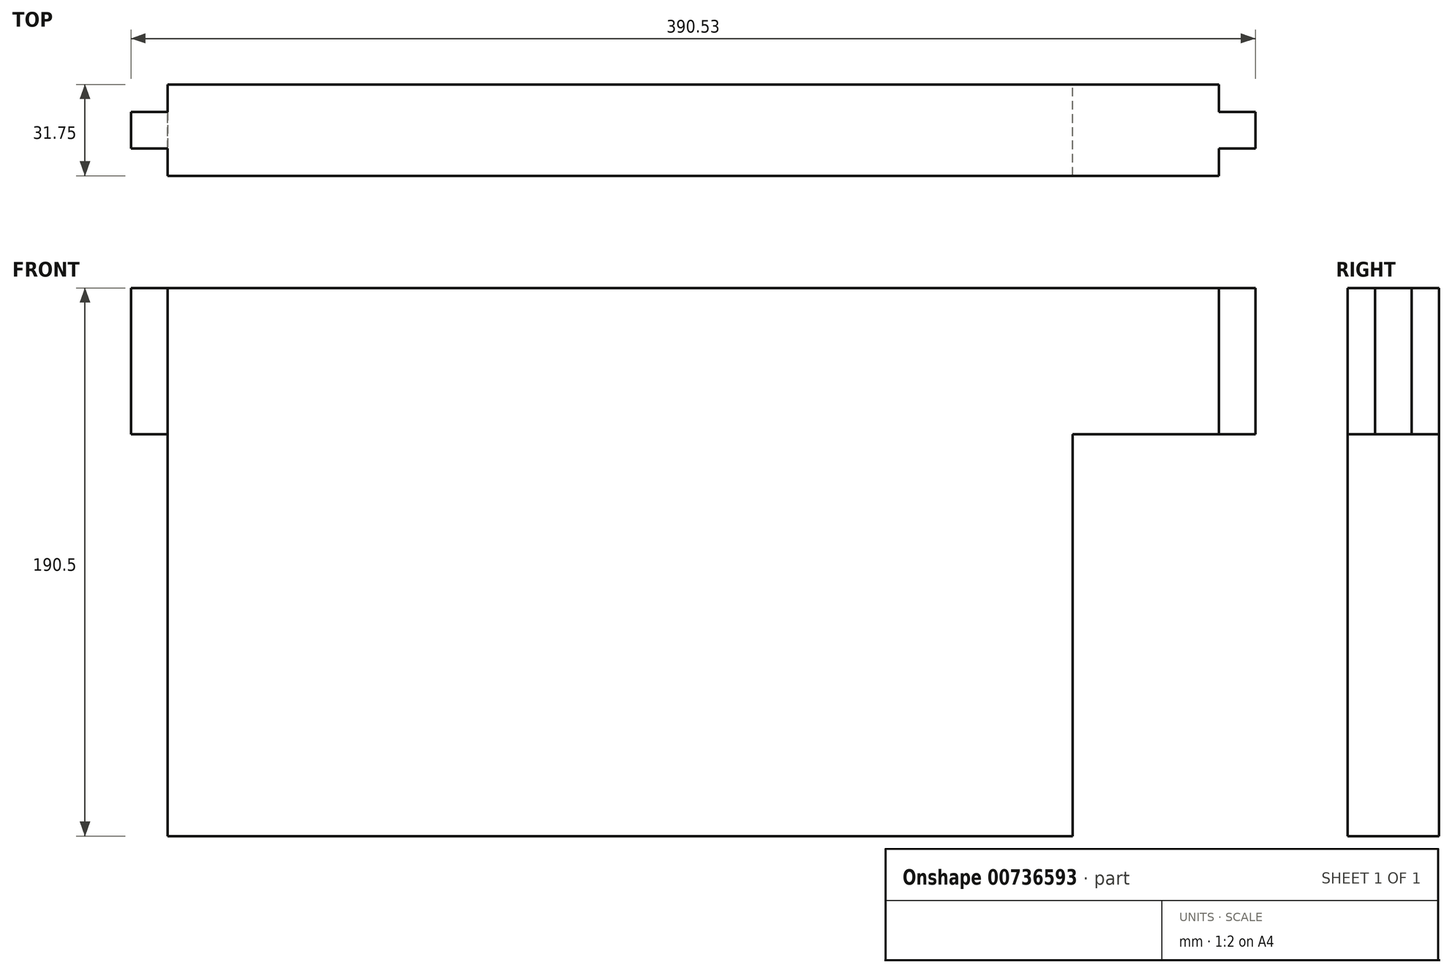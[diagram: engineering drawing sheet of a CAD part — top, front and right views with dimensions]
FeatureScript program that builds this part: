
annotation { "Feature Type Name" : "Feature", "Feature Type Description" : "" }
export const myFeature = defineFeature(function(context is Context, id is Id, definition is map)
    precondition{}
    {
        {
            var Q0;
            Q0=qCreatedBy(makeId("Front.planeOp"),FACE);
            var sketch = newSketch(context, id + "F0", { "sketchPlane" : qUnion([Q0])});
            skLineSegment(sketch, "E0.bottom", {"start": v(-218.9, 99.42) * mm, "end": v(146.23, 99.42) * mm});
            skLineSegment(sketch, "E0.top", {"start": v(-218.9, -91.08) * mm, "end": v(146.23, -91.08) * mm});
            skLineSegment(sketch, "E0.left", {"start": v(-218.9, 99.42) * mm, "end": v(-218.9, -91.08) * mm});
            skLineSegment(sketch, "E0.right", {"start": v(146.23, 99.42) * mm, "end": v(146.23, -91.08) * mm});
            skLineSegment(sketch, "E1.bottom", {"start": v(146.23, -91.08) * mm, "end": v(95.43, -91.08) * mm});
            skLineSegment(sketch, "E1.top", {"start": v(146.23, 48.62) * mm, "end": v(95.43, 48.62) * mm});
            skLineSegment(sketch, "E1.left", {"start": v(146.23, -91.08) * mm, "end": v(146.23, 48.62) * mm});
            skLineSegment(sketch, "E1.right", {"start": v(95.43, -91.08) * mm, "end": v(95.43, 48.62) * mm});
            skSolve(sketch);
        }
        {
            var Q0;
            Q0=makeQuery(id+"F0.imprint","IMPRINT",FACE,{"disambiguationData":[TD([[makeQuery(id+"F0.imprint","IMPRINT",EDGE,{"derivedFrom":sQuery(id+"F0.wireOp",EDGE,"E0.bottom")}),-1.0]])]});
            extrude(context, id + "F1", {"entities" : qUnion([Q0]), "depth" : 31.75 * mm, "offsetDistance" : 25.4 * mm});
        }
        {
            var Q0;
            Q0=makeQuery(id+"F1.opExtrude","SWEPT_FACE",FACE,{"disambiguationData":[OSD([sQuery(id+"F0.wireOp",EDGE,"E0.right")])]});
            var sketch = newSketch(context, id + "F2", { "sketchPlane" : qUnion([Q0])});
            skLineSegment(sketch, "E2.bottom", {"start": v(-22.23, 99.42) * mm, "end": v(-9.53, 99.42) * mm});
            skLineSegment(sketch, "E2.top", {"start": v(-22.23, 48.62) * mm, "end": v(-9.52, 48.62) * mm});
            skLineSegment(sketch, "E2.left", {"start": v(-22.23, 99.42) * mm, "end": v(-22.23, 48.62) * mm});
            skLineSegment(sketch, "E2.right", {"start": v(-9.53, 99.42) * mm, "end": v(-9.52, 48.62) * mm});
            skSolve(sketch);
        }
        {
            var Q0;
            Q0=makeQuery(id+"F2.imprint","IMPRINT",FACE,{"disambiguationData":[TD([[makeQuery(id+"F2.imprint","IMPRINT",EDGE,{"derivedFrom":sQuery(id+"F2.wireOp",EDGE,"E2.bottom")}),-1.0]])]});
            extrude(context, id + "F3", {"entities" : qUnion([Q0]), "operationType" : NewBodyOperationType.ADD, "depth" : 12.7 * mm, "offsetDistance" : 25.4 * mm});
        }
        {
            var Q0;
            Q0=makeQuery(id+"F1.opExtrude","SWEPT_FACE",FACE,{"disambiguationData":[OSD([sQuery(id+"F0.wireOp",EDGE,"E0.left")])]});
            var sketch = newSketch(context, id + "F4", { "sketchPlane" : qUnion([Q0])});
            skLineSegment(sketch, "E3.bottom", {"start": v(9.52, 99.42) * mm, "end": v(22.23, 99.42) * mm});
            skLineSegment(sketch, "E3.top", {"start": v(9.53, 48.62) * mm, "end": v(22.23, 48.62) * mm});
            skLineSegment(sketch, "E3.left", {"start": v(9.52, 99.42) * mm, "end": v(9.53, 48.62) * mm});
            skLineSegment(sketch, "E3.right", {"start": v(22.23, 99.42) * mm, "end": v(22.23, 48.62) * mm});
            skSolve(sketch);
        }
        {
            var Q0;
            Q0=makeQuery(id+"F4.imprint","IMPRINT",FACE,{"disambiguationData":[TD([[makeQuery(id+"F4.imprint","IMPRINT",EDGE,{"derivedFrom":sQuery(id+"F4.wireOp",EDGE,"E3.bottom")}),1.0]])]});
            extrude(context, id + "F5", {"entities" : qUnion([Q0]), "operationType" : NewBodyOperationType.ADD, "depth" : 12.7 * mm, "offsetDistance" : 25.4 * mm});
        }
    });
